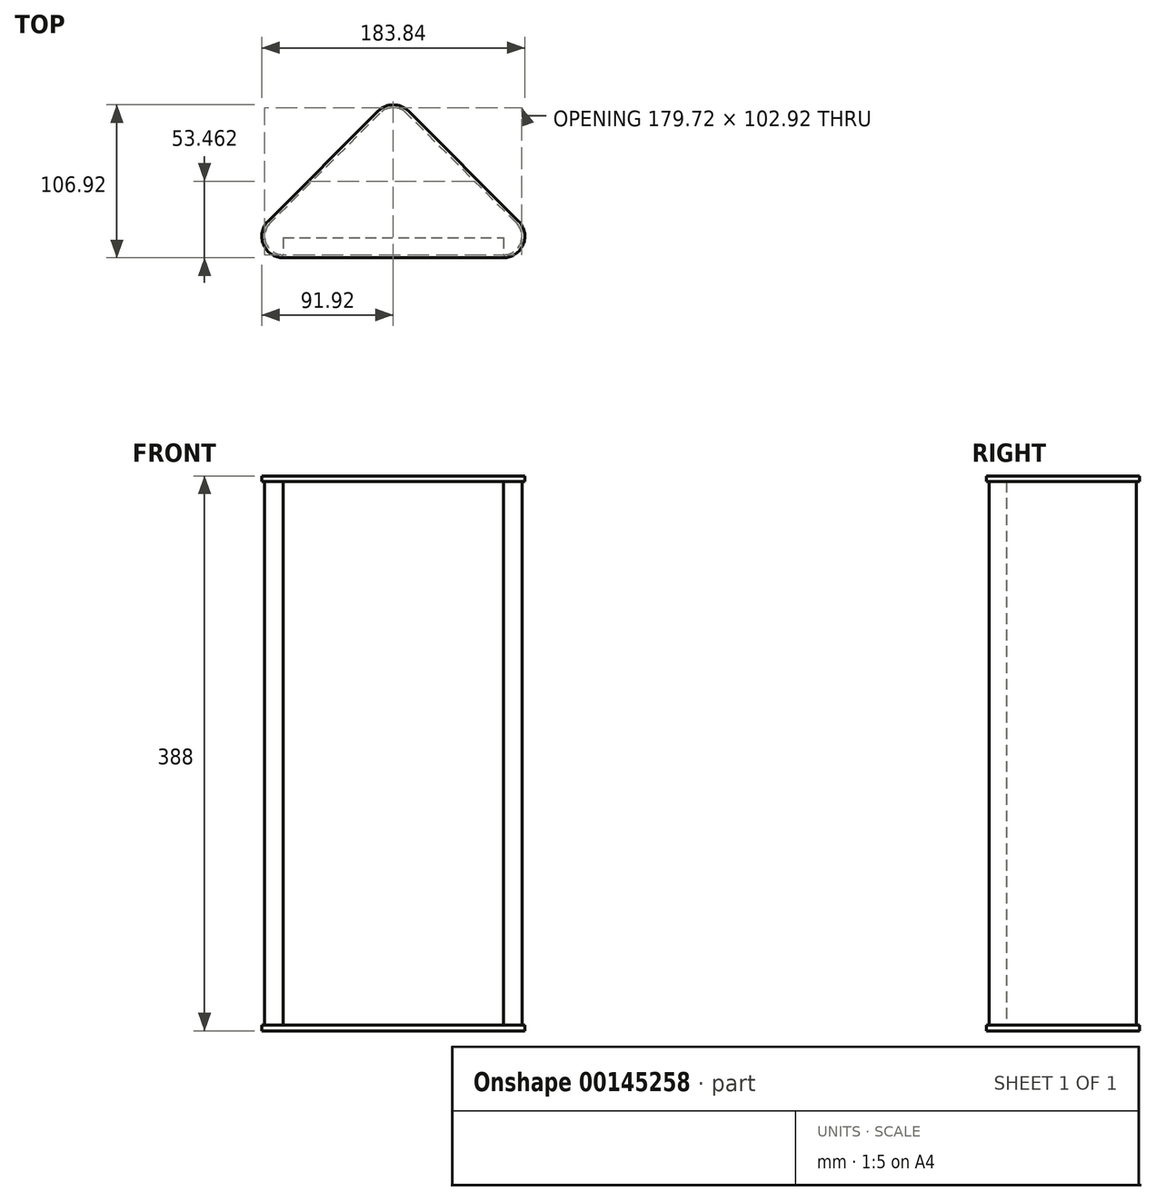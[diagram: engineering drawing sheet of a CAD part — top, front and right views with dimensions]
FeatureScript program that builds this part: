
annotation { "Feature Type Name" : "Feature", "Feature Type Description" : "" }
export const myFeature = defineFeature(function(context is Context, id is Id, definition is map)
    precondition{}
    {
        {
            var Q0;
            Q0=qCreatedBy(makeId("Top.planeOp"),FACE);
            var sketch = newSketch(context, id + "F0", { "sketchPlane" : qUnion([Q0])});
            skLineSegment(sketch, "E0", {"start": v(-113.14, -50) * mm, "end": v(113.14, -50) * mm});
            skLineSegment(sketch, "E1", {"start": v(113.14, -50) * mm, "end": v(0, 63.14) * mm});
            skLineSegment(sketch, "E2", {"start": v(0, 63.14) * mm, "end": v(-113.14, -50) * mm});
            skSolve(sketch);
        }
        {
            var Q0;
            Q0 = qSketchRegion(id + "F0", true);
            extrude(context, id + "F1", {"entities" : qUnion([Q0]), "depth" : 4 * mm});
        }
        {
            var Q0;
            Q0=makeQuery(id+"F1.opExtrude","SWEPT_EDGE",EDGE,{"disambiguationData":[OSD([sQuery(id+"F0.wireOp",EDGE,"E0"),sQuery(id+"F0.wireOp",EDGE,"E2")])]});
            var Q1;
            Q1=makeQuery(id+"F1.opExtrude","SWEPT_EDGE",EDGE,{"disambiguationData":[OSD([sQuery(id+"F0.wireOp",EDGE,"E0"),sQuery(id+"F0.wireOp",EDGE,"E1")])]});
            var Q2;
            Q2=makeQuery(id+"F1.opExtrude","SWEPT_EDGE",EDGE,{"disambiguationData":[OSD([sQuery(id+"F0.wireOp",EDGE,"E1"),sQuery(id+"F0.wireOp",EDGE,"E2")])]});
            fillet(context, id + "F2", {"entities" : qUnion([Q0, Q1, Q2]), "radius" : 15 * mm, "tangentPropagation" : true, "allowEdgeOverflow" : false});
        }
        {
            var Q0;
            Q0=makeQuery(id+"F1.opExtrude","CAP_FACE",FACE,{"disambiguationData":[OSD([sQuery(id+"F0.wireOp",EDGE,"E0"),sQuery(id+"F0.wireOp",EDGE,"E1"),sQuery(id+"F0.wireOp",EDGE,"E2")])],"isStart":false});
            var sketch = newSketch(context, id + "F3", { "sketchPlane" : qUnion([Q0])});
            skLineSegment(sketch, "E3", {"start": v(0, 60.3) * mm, "end": v(-108.3, -48) * mm});
            skLineSegment(sketch, "E4", {"start": v(-108.3, -48) * mm, "end": v(108.3, -48) * mm});
            skLineSegment(sketch, "E5", {"start": v(108.3, -48) * mm, "end": v(0, 60.3) * mm});
            skSolve(sketch);
        }
        {
            var Q0;
            Q0 = qSketchRegion(id + "F3", true);
            extrude(context, id + "F4", {"entities" : qUnion([Q0]), "operationType" : NewBodyOperationType.ADD, "depth" : 380 * mm});
        }
        {
            var Q0;
            Q0=makeQuery(id+"F4.opExtrude","SWEPT_EDGE",EDGE,{"disambiguationData":[OSD([sQuery(id+"F3.wireOp",EDGE,"E4"),sQuery(id+"F3.wireOp",EDGE,"E5")])]});
            var Q1;
            Q1=makeQuery(id+"F4.opExtrude","SWEPT_EDGE",EDGE,{"disambiguationData":[OSD([sQuery(id+"F3.wireOp",EDGE,"E3"),sQuery(id+"F3.wireOp",EDGE,"E4")])]});
            var Q2;
            Q2=makeQuery(id+"F4.opExtrude","SWEPT_EDGE",EDGE,{"disambiguationData":[OSD([sQuery(id+"F3.wireOp",EDGE,"E3"),sQuery(id+"F3.wireOp",EDGE,"E5")])]});
            fillet(context, id + "F5", {"entities" : qUnion([Q0, Q1, Q2]), "radius" : 13 * mm, "tangentPropagation" : true, "allowEdgeOverflow" : false});
        }
        {
            var Q0;
            Q0=makeQuery(id+"F4.opExtrude","CAP_FACE",FACE,{"disambiguationData":[OSD([sQuery(id+"F3.wireOp",EDGE,"E3"),sQuery(id+"F3.wireOp",EDGE,"E4"),sQuery(id+"F3.wireOp",EDGE,"E5")])],"isStart":false});
            var sketch = newSketch(context, id + "F6", { "sketchPlane" : qUnion([Q0])});
            skLineSegment(sketch, "E6", {"start": v(-113.14, -50) * mm, "end": v(0, 63.14) * mm});
            skLineSegment(sketch, "E7", {"start": v(0, 63.14) * mm, "end": v(113.14, -50) * mm});
            skLineSegment(sketch, "E8", {"start": v(113.14, -50) * mm, "end": v(-113.14, -50) * mm});
            skSolve(sketch);
        }
        {
            var Q0;
            Q0 = qSketchRegion(id + "F6", true);
            extrude(context, id + "F7", {"entities" : qUnion([Q0]), "operationType" : NewBodyOperationType.ADD, "depth" : 4 * mm});
        }
        {
            var Q0;
            Q0=makeQuery(id+"F7.opExtrude","SWEPT_EDGE",EDGE,{"disambiguationData":[OSD([sQuery(id+"F6.wireOp",EDGE,"E7"),sQuery(id+"F6.wireOp",EDGE,"E8")])]});
            var Q1;
            Q1=makeQuery(id+"F7.opExtrude","SWEPT_EDGE",EDGE,{"disambiguationData":[OSD([sQuery(id+"F6.wireOp",EDGE,"E6"),sQuery(id+"F6.wireOp",EDGE,"E8")])]});
            var Q2;
            Q2=makeQuery(id+"F7.opExtrude","SWEPT_EDGE",EDGE,{"disambiguationData":[OSD([sQuery(id+"F6.wireOp",EDGE,"E6"),sQuery(id+"F6.wireOp",EDGE,"E7")])]});
            fillet(context, id + "F8", {"entities" : qUnion([Q0, Q1, Q2]), "radius" : 15 * mm, "tangentPropagation" : true, "allowEdgeOverflow" : false});
        }
        {
            var Q0;
            Q0=makeQuery(id+"F4.opExtrude","SWEPT_FACE",FACE,{"disambiguationData":[OSD([sQuery(id+"F3.wireOp",EDGE,"E4")])]});
            var sketch = newSketch(context, id + "F9", { "sketchPlane" : qUnion([Q0])});
            skLineSegment(sketch, "E9.bottom", {"start": v(-76.92, 4) * mm, "end": v(76.92, 4) * mm});
            skLineSegment(sketch, "E9.top", {"start": v(-76.92, 384) * mm, "end": v(76.92, 384) * mm});
            skLineSegment(sketch, "E9.left", {"start": v(-76.92, 4) * mm, "end": v(-76.92, 384) * mm});
            skLineSegment(sketch, "E9.right", {"start": v(76.92, 4) * mm, "end": v(76.92, 384) * mm});
            skSolve(sketch);
        }
        {
            var Q0;
            Q0 = qSketchRegion(id + "F9", true);
            extrude(context, id + "F10", {"entities" : qUnion([Q0]), "operationType" : NewBodyOperationType.REMOVE, "oppositeDirection" : true, "depth" : 12 * mm});
        }
    });
